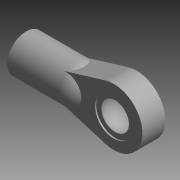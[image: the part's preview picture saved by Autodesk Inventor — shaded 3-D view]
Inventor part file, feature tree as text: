
AUTODESK INVENTOR PART (.ipt)
format: ipt  version: 2014 SP1 (Build 180222100, 222)  size: 123,392 bytes
history: native  units: in
note: dims shown in document units (in); Inventor stores cm internally (conversion verified against a paired STEP export)
features: sketch x5, extrude x4, revolve x1, fillet x1, boolean_combine x1
ambient origin geometry x8: Origin, YZ Plane, XZ Plane, XY Plane, X Axis, Y Axis, Z Axis, Center Point
bodies: Solid1 (feature_tree), Solid2 (feature_tree)
feature tree (12):
  sketch  "Sketch1"  dims[d0=0.4193in d2=0.2756in]
  extrude  "Extrusion1"  Depth=0.2756in
  extrude  "Extrusion2"  Depth=0.1673in
  revolve  "Revolution1"  [1 undecoded]
  extrude  "Extrusion3"  Depth=0.2756in
  extrude  "Extrusion4"  Depth=0.2096in TaperAngle=0.0deg
  fillet  "Fillet1"  Radius=0.1378in
  boolean_combine  "Combine1"
  sketch  "Sketch2"  dims[d3=0.1673in d4=0.0in d5=0.2756in]
  sketch  "Sketch3"  dims[d6=0.1476in d7=0.0in d8=0.25in]
  sketch  "Sketch4"  dims[d9=360.0deg d10=0.2756in]
  sketch  "Sketch5"  dims[d11=0.3937in d12=0.0in d13=0.2096in d14=0.0in d15=0.1378in]
note: 1 required parameter value undecoded (feature->parameter linkage not recoverable at this tier; creation-order binding heuristic only, values carry confidence <= 0.55)
